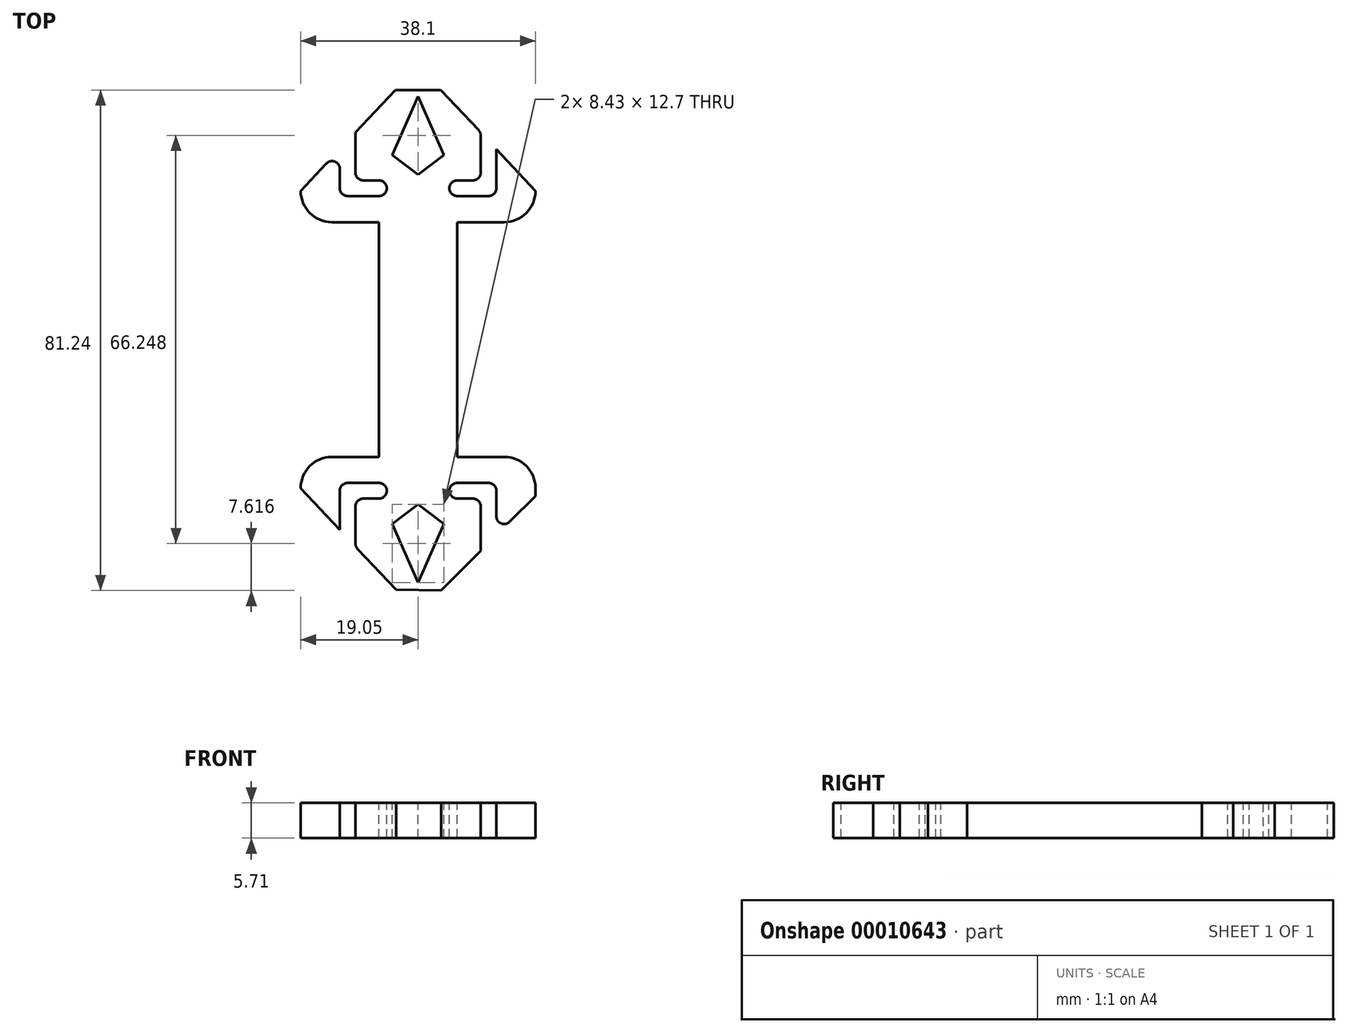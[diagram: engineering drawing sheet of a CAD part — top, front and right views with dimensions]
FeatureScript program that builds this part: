
annotation { "Feature Type Name" : "Feature", "Feature Type Description" : "" }
export const myFeature = defineFeature(function(context is Context, id is Id, definition is map)
    precondition{}
    {
        {
            var Q0;
            Q0=qCreatedBy(makeId("Top.planeOp"),FACE);
            var sketch = newSketch(context, id + "F0", { "sketchPlane" : qUnion([Q0])});
            skLineSegment(sketch, "E0.rect.bottom", {"start": v(-19.05, 25.4) * mm, "end": v(19.05, 25.4) * mm, "construction": true});
            skLineSegment(sketch, "E0.rect.top", {"start": v(-19.05, -25.4) * mm, "end": v(19.05, -25.4) * mm, "construction": true});
            skLineSegment(sketch, "E0.rect.left", {"start": v(-19.05, 25.4) * mm, "end": v(-19.05, -25.4) * mm, "construction": true});
            skLineSegment(sketch, "E0.rect.right", {"start": v(19.05, 25.4) * mm, "end": v(19.05, -25.4) * mm, "construction": true});
            skPoint(sketch, "E0.rect.middle", {"position": v(0, 0) * mm});
            skLineSegment(sketch, "E1", {"start": v(-19.05, 25.4) * mm, "end": v(-19.05, -25.4) * mm});
            skArc(sketch, "E2", {"start": v(-19.05, -25.4) * mm, "mid": v(0, -44.45) * mm, "end": v(19.05, -25.4) * mm});
            skLineSegment(sketch, "E3", {"start": v(19.05, -25.4) * mm, "end": v(19.05, 25.4) * mm});
            skArc(sketch, "E4", {"start": v(19.05, 25.4) * mm, "mid": v(0, 44.45) * mm, "end": v(-19.05, 25.4) * mm});
            skSolve(sketch);
        }
        {
            var Q0;
            Q0 = qSketchRegion(id + "F0", true);
            extrude(context, id + "F1", {"entities" : qUnion([Q0]), "depth" : 5.7 * mm});
        }
        {
            var Q0;
            Q0=makeQuery(id+"F1.opExtrude","CAP_FACE",FACE,{"disambiguationData":[OSD([sQuery(id+"F0.wireOp",EDGE,"E1"),sQuery(id+"F0.wireOp",EDGE,"E2"),sQuery(id+"F0.wireOp",EDGE,"E3"),sQuery(id+"F0.wireOp",EDGE,"E4")])],"isStart":false});
            var sketch = newSketch(context, id + "F2", { "sketchPlane" : qUnion([Q0])});
            skLineSegment(sketch, "E5.rect.bottom", {"start": v(-6.35, 19.05) * mm, "end": v(-31.75, 19.05) * mm});
            skLineSegment(sketch, "E5.rect.top", {"start": v(-6.35, -19.05) * mm, "end": v(-31.75, -19.05) * mm});
            skLineSegment(sketch, "E5.rect.left", {"start": v(-6.35, 19.05) * mm, "end": v(-6.35, -19.05) * mm});
            skLineSegment(sketch, "E5.rect.right", {"start": v(-31.75, 19.05) * mm, "end": v(-31.75, -19.05) * mm});
            skPoint(sketch, "E5.rect.middle", {"position": v(-19.05, 0) * mm});
            skLineSegment(sketch, "E6.rect.bottom", {"start": v(6.35, 19.05) * mm, "end": v(31.75, 19.05) * mm});
            skLineSegment(sketch, "E6.rect.top", {"start": v(6.35, -19.05) * mm, "end": v(31.75, -19.05) * mm});
            skLineSegment(sketch, "E6.rect.left", {"start": v(6.35, 19.05) * mm, "end": v(6.35, -19.05) * mm});
            skLineSegment(sketch, "E6.rect.right", {"start": v(31.75, 19.05) * mm, "end": v(31.75, -19.05) * mm});
            skPoint(sketch, "E6.rect.middle", {"position": v(19.05, 0) * mm});
            skSolve(sketch);
        }
        {
            var Q0;
            Q0 = qSketchRegion(id + "F2", true);
            extrude(context, id + "F3", {"entities" : qUnion([Q0]), "operationType" : NewBodyOperationType.REMOVE, "oppositeDirection" : true, "depth" : 25.4 * mm});
        }
        {
            var Q0;
            Q0=makeQuery(id+"F3.boolean.opBoolean","INTERSECT",EDGE,{"derivedFrom":[makeQuery(id+"F1.opExtrude","SWEPT_FACE",FACE,{"disambiguationData":[OSD([sQuery(id+"F0.wireOp",EDGE,"E1")])]}),makeQuery(id+"F3.opExtrude","SWEPT_FACE",FACE,{"disambiguationData":[OSD([sQuery(id+"F2.wireOp",EDGE,"E5.rect.bottom")])]})]});
            var Q1;
            Q1=makeQuery(id+"F3.boolean.opBoolean","INTERSECT",EDGE,{"derivedFrom":[makeQuery(id+"F1.opExtrude","SWEPT_FACE",FACE,{"disambiguationData":[OSD([sQuery(id+"F0.wireOp",EDGE,"E3")])]}),makeQuery(id+"F3.opExtrude","SWEPT_FACE",FACE,{"disambiguationData":[OSD([sQuery(id+"F2.wireOp",EDGE,"E6.rect.bottom")])]})]});
            var Q2;
            Q2=makeQuery(id+"F3.boolean.opBoolean","INTERSECT",EDGE,{"derivedFrom":[makeQuery(id+"F1.opExtrude","SWEPT_FACE",FACE,{"disambiguationData":[OSD([sQuery(id+"F0.wireOp",EDGE,"E3")])]}),makeQuery(id+"F3.opExtrude","SWEPT_FACE",FACE,{"disambiguationData":[OSD([sQuery(id+"F2.wireOp",EDGE,"E6.rect.top")])]})]});
            var Q3;
            Q3=makeQuery(id+"F3.boolean.opBoolean","INTERSECT",EDGE,{"derivedFrom":[makeQuery(id+"F1.opExtrude","SWEPT_FACE",FACE,{"disambiguationData":[OSD([sQuery(id+"F0.wireOp",EDGE,"E1")])]}),makeQuery(id+"F3.opExtrude","SWEPT_FACE",FACE,{"disambiguationData":[OSD([sQuery(id+"F2.wireOp",EDGE,"E5.rect.top")])]})]});
            fillet(context, id + "F4", {"entities" : qUnion([Q0, Q1, Q2, Q3]), "radius" : 5.08 * mm, "tangentPropagation" : true, "allowEdgeOverflow" : false});
        }
        {
            var Q0;
            Q0=makeQuery(id+"F1.opExtrude","CAP_FACE",FACE,{"disambiguationData":[OSD([sQuery(id+"F0.wireOp",EDGE,"E1"),sQuery(id+"F0.wireOp",EDGE,"E2"),sQuery(id+"F0.wireOp",EDGE,"E3"),sQuery(id+"F0.wireOp",EDGE,"E4")])],"isStart":true});
            var sketch = newSketch(context, id + "F5", { "sketchPlane" : qUnion([Q0])});
            skLineSegment(sketch, "E7", {"start": v(0, -44.45) * mm, "end": v(-19.05, -24.13) * mm});
            skLineSegment(sketch, "E8", {"start": v(-19.05, -24.13) * mm, "end": v(-32.8, -24.13) * mm});
            skLineSegment(sketch, "E9", {"start": v(-32.8, -24.13) * mm, "end": v(-31.63, -69.02) * mm});
            skLineSegment(sketch, "E10", {"start": v(-31.63, -69.02) * mm, "end": v(6.8, -79.96) * mm});
            skLineSegment(sketch, "E11", {"start": v(6.8, -79.96) * mm, "end": v(33.12, -33.25) * mm});
            skLineSegment(sketch, "E12", {"start": v(33.12, -33.25) * mm, "end": v(33.71, -15.5) * mm});
            skLineSegment(sketch, "E13", {"start": v(33.71, -15.5) * mm, "end": v(19.05, -24.13) * mm});
            skLineSegment(sketch, "E14", {"start": v(19.05, -24.13) * mm, "end": v(0, -44.45) * mm});
            skLineSegment(sketch, "E15", {"start": v(-19.05, 24.13) * mm, "end": v(0, 44.45) * mm});
            skLineSegment(sketch, "E16", {"start": v(0, 44.45) * mm, "end": v(19.05, 25.4) * mm});
            skLineSegment(sketch, "E17", {"start": v(19.05, 25.4) * mm, "end": v(30, 21.66) * mm});
            skLineSegment(sketch, "E18", {"start": v(30, 21.66) * mm, "end": v(0, 67.23) * mm});
            skLineSegment(sketch, "E19", {"start": v(0, 67.23) * mm, "end": v(-17.28, 60.86) * mm});
            skLineSegment(sketch, "E20", {"start": v(-17.28, 60.86) * mm, "end": v(-24.76, 43.8) * mm});
            skLineSegment(sketch, "E21", {"start": v(-24.76, 43.8) * mm, "end": v(-19.05, 24.13) * mm});
            skSolve(sketch);
        }
        {
            var Q0;
            Q0 = qSketchRegion(id + "F5", true);
            extrude(context, id + "F6", {"entities" : qUnion([Q0]), "operationType" : NewBodyOperationType.REMOVE, "oppositeDirection" : true, "depth" : 25.4 * mm});
        }
        {
            var Q0;
            Q0=makeQuery(id+"F6.boolean.opBoolean","COPY",EDGE,{"derivedFrom":makeQuery(id+"F6.opExtrude","SWEPT_EDGE",EDGE,{"disambiguationData":[OSD([sQuery(id+"F0.wireOp",EDGE,"E4"),sQuery(id+"F5.wireOp",EDGE,"E7"),sQuery(id+"F5.wireOp",EDGE,"E14")])]})});
            var Q1;
            Q1=makeQuery(id+"F6.boolean.opBoolean","COPY",EDGE,{"derivedFrom":makeQuery(id+"F6.opExtrude","SWEPT_EDGE",EDGE,{"disambiguationData":[OSD([sQuery(id+"F0.wireOp",EDGE,"E2"),sQuery(id+"F5.wireOp",EDGE,"E15"),sQuery(id+"F5.wireOp",EDGE,"E16")])]})});
            chamfer(context, id + "F7", {"entities" : qUnion([Q0, Q1]), "width" : 5.08 * mm, "tangentPropagation" : true});
        }
        {
            var Q0;
            Q0=makeQuery(id+"F1.opExtrude","CAP_FACE",FACE,{"disambiguationData":[OSD([sQuery(id+"F0.wireOp",EDGE,"E1"),sQuery(id+"F0.wireOp",EDGE,"E2"),sQuery(id+"F0.wireOp",EDGE,"E3"),sQuery(id+"F0.wireOp",EDGE,"E4")])],"isStart":false});
            var sketch = newSketch(context, id + "F8", { "sketchPlane" : qUnion([Q0])});
            skLineSegment(sketch, "E22", {"start": v(-10.16, 33.61) * mm, "end": v(-10.16, 25.82) * mm});
            skLineSegment(sketch, "E23", {"start": v(-10.16, 25.82) * mm, "end": v(-6.35, 25.82) * mm});
            skArc(sketch, "E24", {"start": v(-6.35, 23.28) * mm, "mid": v(-5.08, 24.55) * mm, "end": v(-6.35, 25.82) * mm});
            skLineSegment(sketch, "E25", {"start": v(-6.35, 23.28) * mm, "end": v(-12.7, 23.28) * mm});
            skLineSegment(sketch, "E26", {"start": v(-12.7, 23.28) * mm, "end": v(-12.7, 30.9) * mm});
            skLineSegment(sketch, "E27", {"start": v(-12.7, 30.9) * mm, "end": v(-10.16, 33.61) * mm});
            skLineSegment(sketch, "E28", {"start": v(0, 40.74) * mm, "end": v(0, -40.92) * mm, "construction": true});
            skLineSegment(sketch, "E29", {"start": v(-6.35, 0) * mm, "end": v(6.35, 0) * mm, "construction": true});
            skLineSegment(sketch, "E30.0.MirrorCS", {"start": v(10.16, 33.61) * mm, "end": v(10.16, 25.82) * mm});
            skLineSegment(sketch, "E30.1.MirrorCS", {"start": v(10.16, 25.82) * mm, "end": v(6.35, 25.82) * mm});
            skLineSegment(sketch, "E30.2.MirrorCS", {"start": v(12.7, 30.9) * mm, "end": v(10.16, 33.61) * mm});
            skArc(sketch, "E30.3.MirrorCS", {"start": v(6.35, 23.28) * mm, "mid": v(5.08, 24.55) * mm, "end": v(6.35, 25.82) * mm});
            skLineSegment(sketch, "E30.4.MirrorCS", {"start": v(12.7, 23.28) * mm, "end": v(12.7, 30.9) * mm});
            skLineSegment(sketch, "E30.5.MirrorCS", {"start": v(6.35, 23.28) * mm, "end": v(12.7, 23.28) * mm});
            skLineSegment(sketch, "E31.0.MirrorCS", {"start": v(-12.7, -30.9) * mm, "end": v(-10.16, -33.61) * mm});
            skLineSegment(sketch, "E31.1.MirrorCS", {"start": v(-12.7, -23.28) * mm, "end": v(-12.7, -30.9) * mm});
            skLineSegment(sketch, "E31.2.MirrorCS", {"start": v(-6.35, -23.28) * mm, "end": v(-12.7, -23.28) * mm});
            skArc(sketch, "E31.3.MirrorCS", {"start": v(-6.35, -23.28) * mm, "mid": v(-5.08, -24.55) * mm, "end": v(-6.35, -25.82) * mm});
            skLineSegment(sketch, "E31.4.MirrorCS", {"start": v(-10.16, -25.82) * mm, "end": v(-6.35, -25.82) * mm});
            skLineSegment(sketch, "E31.5.MirrorCS", {"start": v(-10.16, -33.61) * mm, "end": v(-10.16, -25.82) * mm});
            skLineSegment(sketch, "E31.6.MirrorCS", {"start": v(6.35, -23.28) * mm, "end": v(12.7, -23.28) * mm});
            skLineSegment(sketch, "E31.7.MirrorCS", {"start": v(10.16, -33.61) * mm, "end": v(10.16, -25.82) * mm});
            skLineSegment(sketch, "E31.8.MirrorCS", {"start": v(12.7, -30.9) * mm, "end": v(10.16, -33.61) * mm});
            skLineSegment(sketch, "E31.9.MirrorCS", {"start": v(12.7, -23.28) * mm, "end": v(12.7, -30.9) * mm});
            skLineSegment(sketch, "E31.10.MirrorCS", {"start": v(10.16, -25.82) * mm, "end": v(6.35, -25.82) * mm});
            skArc(sketch, "E31.11.MirrorCS", {"start": v(6.35, -23.28) * mm, "mid": v(5.08, -24.55) * mm, "end": v(6.35, -25.82) * mm});
            skSolve(sketch);
        }
        {
            var Q0;
            Q0 = qSketchRegion(id + "F8", true);
            extrude(context, id + "F9", {"entities" : qUnion([Q0]), "operationType" : NewBodyOperationType.REMOVE, "oppositeDirection" : true, "depth" : 25.4 * mm});
        }
        {
            var Q0;
            Q0=makeQuery(id+"F1.opExtrude","CAP_FACE",FACE,{"disambiguationData":[OSD([sQuery(id+"F0.wireOp",EDGE,"E1"),sQuery(id+"F0.wireOp",EDGE,"E2"),sQuery(id+"F0.wireOp",EDGE,"E3"),sQuery(id+"F0.wireOp",EDGE,"E4")])],"isStart":false});
            var sketch = newSketch(context, id + "F10", { "sketchPlane" : qUnion([Q0])});
            skLineSegment(sketch, "E32", {"start": v(10.16, -33.61) * mm, "end": v(10.16, -34.3) * mm});
            skLineSegment(sketch, "E33", {"start": v(10.16, -34.3) * mm, "end": v(12.7, -31.75) * mm});
            skLineSegment(sketch, "E34", {"start": v(12.7, -31.75) * mm, "end": v(12.7, -30.9) * mm});
            skLineSegment(sketch, "E35", {"start": v(12.7, -30.9) * mm, "end": v(10.16, -33.61) * mm});
            skSolve(sketch);
        }
        {
            var Q0;
            Q0 = qSketchRegion(id + "F10", true);
            extrude(context, id + "F11", {"entities" : qUnion([Q0]), "operationType" : NewBodyOperationType.REMOVE, "oppositeDirection" : true, "depth" : 25.4 * mm});
        }
        {
            var Q0;
            Q0=makeQuery(id+"F9.boolean.opBoolean","COPY",EDGE,{"derivedFrom":makeQuery(id+"F9.opExtrude","SWEPT_EDGE",EDGE,{"disambiguationData":[OSD([sQuery(id+"F0.wireOp",EDGE,"E1"),sQuery(id+"F0.wireOp",EDGE,"E2"),sQuery(id+"F0.wireOp",EDGE,"E3"),sQuery(id+"F0.wireOp",EDGE,"E4"),sQuery(id+"F5.wireOp",EDGE,"E14"),sQuery(id+"F8.wireOp",EDGE,"E30.2.MirrorCS"),sQuery(id+"F8.wireOp",EDGE,"E30.4.MirrorCS")])]})});
            var Q1;
            Q1=makeQuery(id+"F9.boolean.opBoolean","COPY",EDGE,{"derivedFrom":makeQuery(id+"F9.opExtrude","SWEPT_EDGE",EDGE,{"disambiguationData":[OSD([sQuery(id+"F0.wireOp",EDGE,"E1"),sQuery(id+"F0.wireOp",EDGE,"E2"),sQuery(id+"F0.wireOp",EDGE,"E3"),sQuery(id+"F0.wireOp",EDGE,"E4"),sQuery(id+"F5.wireOp",EDGE,"E7"),sQuery(id+"F8.wireOp",EDGE,"E26"),sQuery(id+"F8.wireOp",EDGE,"E27")])]})});
            var Q2;
            Q2=makeQuery(id+"F11.boolean.opBoolean","COPY",EDGE,{"derivedFrom":makeQuery(id+"F11.opExtrude","SWEPT_EDGE",EDGE,{"disambiguationData":[OSD([sQuery(id+"F0.wireOp",EDGE,"E1"),sQuery(id+"F0.wireOp",EDGE,"E2"),sQuery(id+"F0.wireOp",EDGE,"E3"),sQuery(id+"F0.wireOp",EDGE,"E4"),sQuery(id+"F5.wireOp",EDGE,"E16"),sQuery(id+"F10.wireOp",EDGE,"E33"),sQuery(id+"F10.wireOp",EDGE,"E34")])]})});
            var Q3;
            Q3=makeQuery(id+"F9.boolean.opBoolean","COPY",EDGE,{"derivedFrom":makeQuery(id+"F9.opExtrude","SWEPT_EDGE",EDGE,{"disambiguationData":[OSD([sQuery(id+"F0.wireOp",EDGE,"E1"),sQuery(id+"F0.wireOp",EDGE,"E2"),sQuery(id+"F0.wireOp",EDGE,"E3"),sQuery(id+"F0.wireOp",EDGE,"E4"),sQuery(id+"F5.wireOp",EDGE,"E15"),sQuery(id+"F8.wireOp",EDGE,"E31.0.MirrorCS"),sQuery(id+"F8.wireOp",EDGE,"E31.1.MirrorCS")])]})});
            var Q4;
            Q4=makeQuery(id+"F9.boolean.opBoolean","COPY",EDGE,{"derivedFrom":makeQuery(id+"F9.opExtrude","SWEPT_EDGE",EDGE,{"disambiguationData":[OSD([sQuery(id+"F0.wireOp",EDGE,"E1"),sQuery(id+"F0.wireOp",EDGE,"E2"),sQuery(id+"F0.wireOp",EDGE,"E3"),sQuery(id+"F0.wireOp",EDGE,"E4"),sQuery(id+"F5.wireOp",EDGE,"E7"),sQuery(id+"F8.wireOp",EDGE,"E22"),sQuery(id+"F8.wireOp",EDGE,"E27")])]})});
            var Q5;
            Q5=makeQuery(id+"F9.boolean.opBoolean","COPY",EDGE,{"derivedFrom":makeQuery(id+"F9.opExtrude","SWEPT_EDGE",EDGE,{"disambiguationData":[OSD([sQuery(id+"F0.wireOp",EDGE,"E1"),sQuery(id+"F0.wireOp",EDGE,"E2"),sQuery(id+"F0.wireOp",EDGE,"E3"),sQuery(id+"F0.wireOp",EDGE,"E4"),sQuery(id+"F5.wireOp",EDGE,"E14"),sQuery(id+"F8.wireOp",EDGE,"E30.0.MirrorCS"),sQuery(id+"F8.wireOp",EDGE,"E30.2.MirrorCS")])]})});
            var Q6;
            Q6=makeQuery(id+"F9.boolean.opBoolean","COPY",EDGE,{"derivedFrom":makeQuery(id+"F9.opExtrude","SWEPT_EDGE",EDGE,{"disambiguationData":[OSD([sQuery(id+"F8.wireOp",EDGE,"E30.0.MirrorCS"),sQuery(id+"F8.wireOp",EDGE,"E30.1.MirrorCS")])]})});
            var Q7;
            Q7=makeQuery(id+"F9.boolean.opBoolean","COPY",EDGE,{"derivedFrom":makeQuery(id+"F9.opExtrude","SWEPT_EDGE",EDGE,{"disambiguationData":[OSD([sQuery(id+"F8.wireOp",EDGE,"E30.4.MirrorCS"),sQuery(id+"F8.wireOp",EDGE,"E30.5.MirrorCS")])]})});
            var Q8;
            Q8=makeQuery(id+"F9.boolean.opBoolean","COPY",EDGE,{"derivedFrom":makeQuery(id+"F9.opExtrude","SWEPT_EDGE",EDGE,{"disambiguationData":[OSD([sQuery(id+"F8.wireOp",EDGE,"E25"),sQuery(id+"F8.wireOp",EDGE,"E26")])]})});
            var Q9;
            Q9=makeQuery(id+"F9.boolean.opBoolean","COPY",EDGE,{"derivedFrom":makeQuery(id+"F9.opExtrude","SWEPT_EDGE",EDGE,{"disambiguationData":[OSD([sQuery(id+"F8.wireOp",EDGE,"E22"),sQuery(id+"F8.wireOp",EDGE,"E23")])]})});
            var Q10;
            Q10=makeQuery(id+"F9.boolean.opBoolean","COPY",EDGE,{"derivedFrom":makeQuery(id+"F9.opExtrude","SWEPT_EDGE",EDGE,{"disambiguationData":[OSD([sQuery(id+"F0.wireOp",EDGE,"E1"),sQuery(id+"F0.wireOp",EDGE,"E2"),sQuery(id+"F0.wireOp",EDGE,"E3"),sQuery(id+"F0.wireOp",EDGE,"E4"),sQuery(id+"F5.wireOp",EDGE,"E15"),sQuery(id+"F8.wireOp",EDGE,"E31.0.MirrorCS"),sQuery(id+"F8.wireOp",EDGE,"E31.5.MirrorCS")])]})});
            var Q11;
            Q11=makeQuery(id+"F11.boolean.opBoolean","COPY",EDGE,{"derivedFrom":makeQuery(id+"F11.opExtrude","SWEPT_EDGE",EDGE,{"disambiguationData":[OSD([sQuery(id+"F0.wireOp",EDGE,"E1"),sQuery(id+"F0.wireOp",EDGE,"E2"),sQuery(id+"F0.wireOp",EDGE,"E3"),sQuery(id+"F0.wireOp",EDGE,"E4"),sQuery(id+"F5.wireOp",EDGE,"E16"),sQuery(id+"F10.wireOp",EDGE,"E32"),sQuery(id+"F10.wireOp",EDGE,"E33")])]})});
            var Q12;
            Q12=makeQuery(id+"F9.boolean.opBoolean","COPY",EDGE,{"derivedFrom":makeQuery(id+"F9.opExtrude","SWEPT_EDGE",EDGE,{"disambiguationData":[OSD([sQuery(id+"F8.wireOp",EDGE,"E31.1.MirrorCS"),sQuery(id+"F8.wireOp",EDGE,"E31.2.MirrorCS")])]})});
            var Q13;
            Q13=makeQuery(id+"F9.boolean.opBoolean","COPY",EDGE,{"derivedFrom":makeQuery(id+"F9.opExtrude","SWEPT_EDGE",EDGE,{"disambiguationData":[OSD([sQuery(id+"F8.wireOp",EDGE,"E31.4.MirrorCS"),sQuery(id+"F8.wireOp",EDGE,"E31.5.MirrorCS")])]})});
            var Q14;
            Q14=makeQuery(id+"F9.boolean.opBoolean","COPY",EDGE,{"derivedFrom":makeQuery(id+"F9.opExtrude","SWEPT_EDGE",EDGE,{"disambiguationData":[OSD([sQuery(id+"F8.wireOp",EDGE,"E31.6.MirrorCS"),sQuery(id+"F8.wireOp",EDGE,"E31.9.MirrorCS")])]})});
            var Q15;
            Q15=makeQuery(id+"F9.boolean.opBoolean","COPY",EDGE,{"derivedFrom":makeQuery(id+"F9.opExtrude","SWEPT_EDGE",EDGE,{"disambiguationData":[OSD([sQuery(id+"F8.wireOp",EDGE,"E31.7.MirrorCS"),sQuery(id+"F8.wireOp",EDGE,"E31.10.MirrorCS")])]})});
            fillet(context, id + "F12", {"entities" : qUnion([Q0, Q1, Q2, Q3, Q4, Q5, Q6, Q7, Q8, Q9, Q10, Q11, Q12, Q13, Q14, Q15]), "radius" : 1.27 * mm, "tangentPropagation" : true, "allowEdgeOverflow" : false});
        }
        {
            var Q0;
            Q0=makeQuery(id+"F1.opExtrude","CAP_FACE",FACE,{"disambiguationData":[OSD([sQuery(id+"F0.wireOp",EDGE,"E1"),sQuery(id+"F0.wireOp",EDGE,"E2"),sQuery(id+"F0.wireOp",EDGE,"E3"),sQuery(id+"F0.wireOp",EDGE,"E4")])],"isStart":false});
            var sketch = newSketch(context, id + "F13", { "sketchPlane" : qUnion([Q0])});
            skLineSegment(sketch, "E36", {"start": v(0, 40.74) * mm, "end": v(0, -40.97) * mm, "construction": true});
            skLineSegment(sketch, "E37", {"start": v(0, 39.47) * mm, "end": v(-4.21, 29.95) * mm});
            skLineSegment(sketch, "E38", {"start": v(-4.21, 29.95) * mm, "end": v(0, 26.77) * mm});
            skLineSegment(sketch, "E39", {"start": v(0, 39.47) * mm, "end": v(4.21, 29.95) * mm});
            skLineSegment(sketch, "E40", {"start": v(4.21, 29.95) * mm, "end": v(0, 26.77) * mm});
            skLineSegment(sketch, "E41", {"start": v(-4.21, 29.95) * mm, "end": v(4.21, 29.95) * mm, "construction": true});
            skLineSegment(sketch, "E42", {"start": v(-6.35, 0) * mm, "end": v(6.35, 0) * mm, "construction": true});
            skLineSegment(sketch, "E43.0.MirrorCS", {"start": v(0, -39.47) * mm, "end": v(-4.21, -29.95) * mm});
            skLineSegment(sketch, "E43.1.MirrorCS", {"start": v(0, -40.74) * mm, "end": v(0, 40.97) * mm, "construction": true});
            skLineSegment(sketch, "E43.2.MirrorCS", {"start": v(-4.21, -29.95) * mm, "end": v(4.21, -29.95) * mm, "construction": true});
            skLineSegment(sketch, "E43.3.MirrorCS", {"start": v(-4.21, -29.95) * mm, "end": v(0, -26.77) * mm});
            skLineSegment(sketch, "E43.4.MirrorCS", {"start": v(0, -39.47) * mm, "end": v(4.21, -29.95) * mm});
            skLineSegment(sketch, "E43.5.MirrorCS", {"start": v(4.21, -29.95) * mm, "end": v(0, -26.77) * mm});
            skSolve(sketch);
        }
        {
            var Q0;
            Q0 = qSketchRegion(id + "F13", true);
            extrude(context, id + "F14", {"entities" : qUnion([Q0]), "operationType" : NewBodyOperationType.REMOVE, "oppositeDirection" : true, "depth" : 25.4 * mm});
        }
    });
